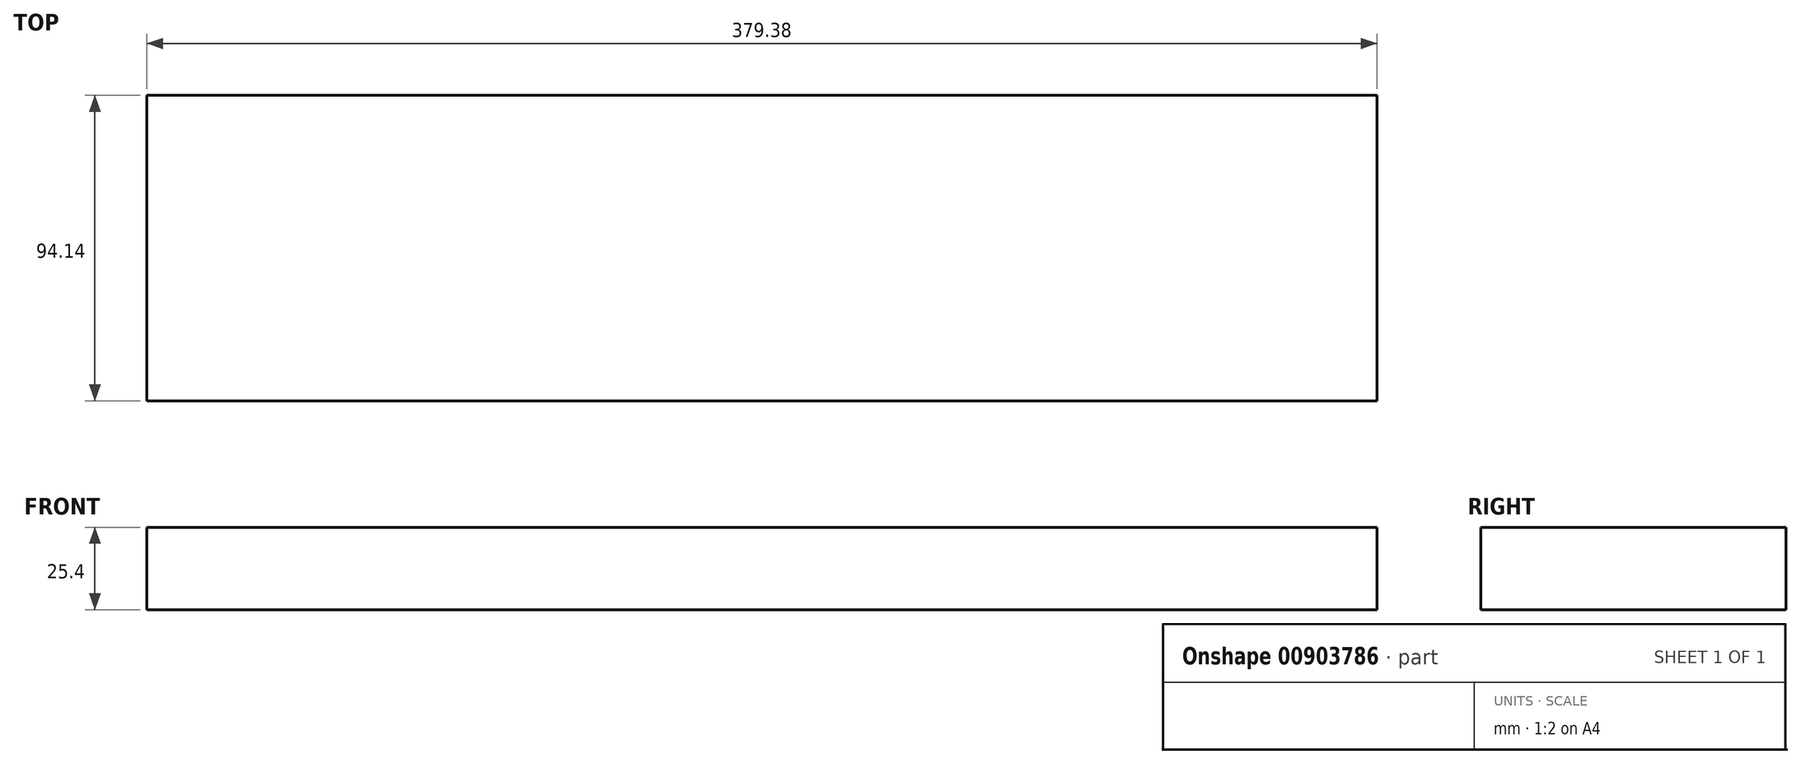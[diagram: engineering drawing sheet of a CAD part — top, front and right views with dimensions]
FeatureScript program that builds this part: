
annotation { "Feature Type Name" : "Feature", "Feature Type Description" : "" }
export const myFeature = defineFeature(function(context is Context, id is Id, definition is map)
    precondition{}
    {
        {
            var Q0;
            Q0=qCreatedBy(makeId("Top.planeOp"),FACE);
            var sketch = newSketch(context, id + "F0", { "sketchPlane" : qUnion([Q0])});
            skLineSegment(sketch, "E0.bottom", {"start": v(120.86, 0) * mm, "end": v(-258.52, 0) * mm});
            skLineSegment(sketch, "E0.top", {"start": v(120.86, 94.14) * mm, "end": v(-258.52, 94.14) * mm});
            skLineSegment(sketch, "E0.left", {"start": v(120.86, 0) * mm, "end": v(120.86, 94.14) * mm});
            skLineSegment(sketch, "E0.right", {"start": v(-258.52, 0) * mm, "end": v(-258.52, 94.14) * mm});
            skPoint(sketch, "E0.middle", {"position": v(-68.83, 47.07) * mm});
            skSolve(sketch);
        }
        {
            var Q0;
            Q0=makeQuery(id+"F0.imprint","IMPRINT",FACE,{"disambiguationData":[TD([[makeQuery(id+"F0.imprint","IMPRINT",EDGE,{"derivedFrom":sQuery(id+"F0.wireOp",EDGE,"E0.bottom")}),-1.0]])]});
            extrude(context, id + "F1", {"entities" : qUnion([Q0]), "depth" : 25.4 * mm, "offsetDistance" : 25.4 * mm});
        }
    });
